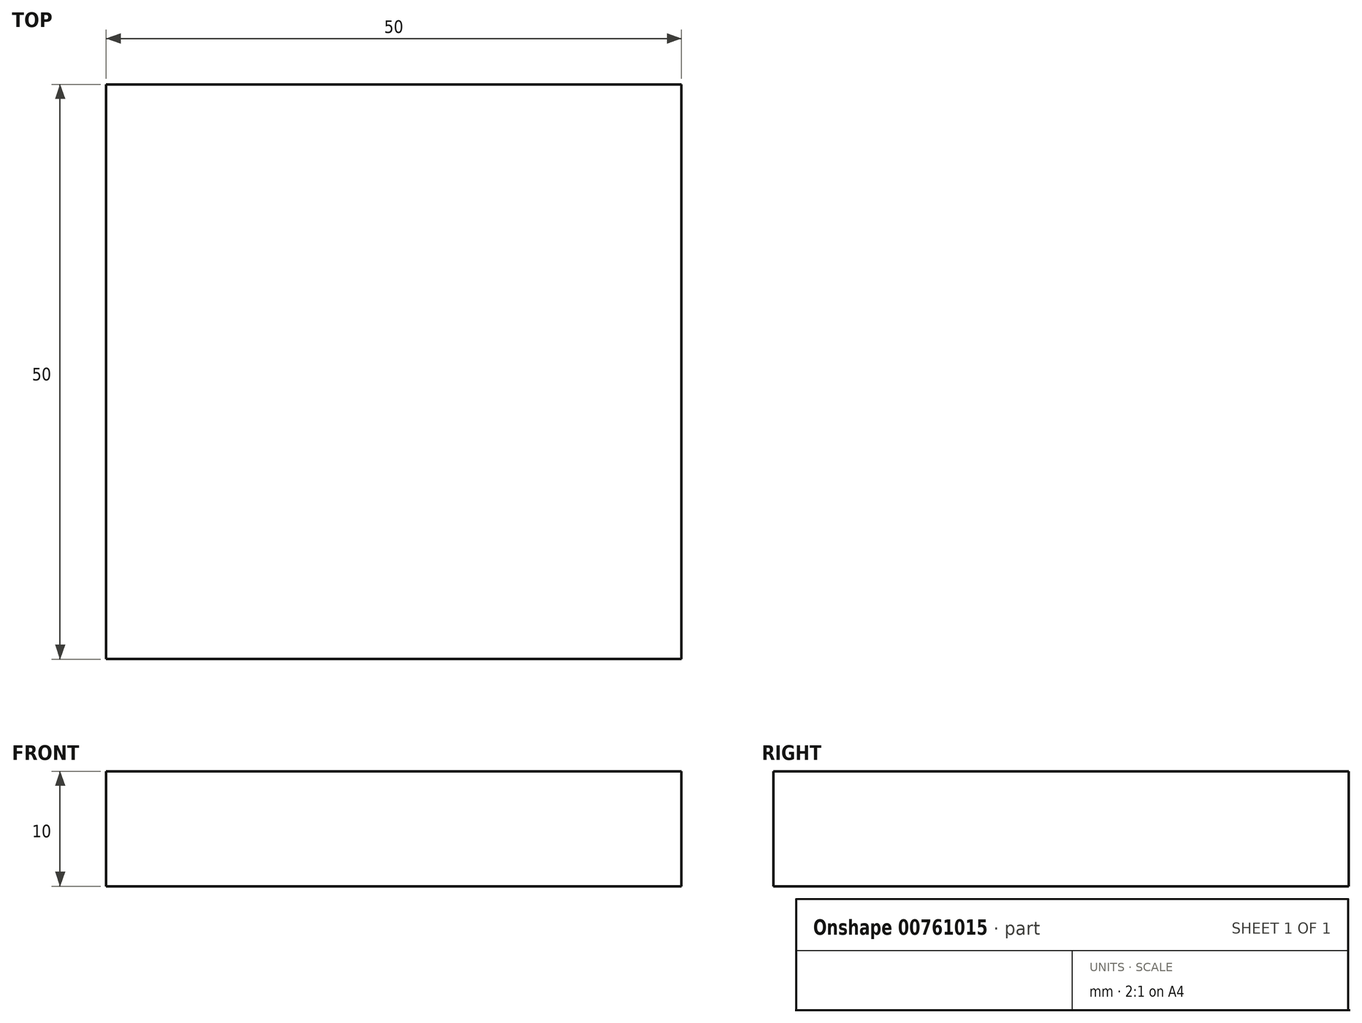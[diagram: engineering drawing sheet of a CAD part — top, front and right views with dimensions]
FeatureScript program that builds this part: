
annotation { "Feature Type Name" : "Feature", "Feature Type Description" : "" }
export const myFeature = defineFeature(function(context is Context, id is Id, definition is map)
    precondition{}
    {
        {
            var Q0;
            Q0=qCreatedBy(makeId("Top.planeOp"),FACE);
            var sketch = newSketch(context, id + "F0", { "sketchPlane" : qUnion([Q0])});
            skLineSegment(sketch, "E0.bottom", {"start": v(-13.93, 17.2) * mm, "end": v(36.07, 17.2) * mm});
            skLineSegment(sketch, "E0.top", {"start": v(-13.93, -32.8) * mm, "end": v(36.07, -32.8) * mm});
            skLineSegment(sketch, "E0.left", {"start": v(-13.93, 17.2) * mm, "end": v(-13.93, -32.8) * mm});
            skLineSegment(sketch, "E0.right", {"start": v(36.07, 17.2) * mm, "end": v(36.07, -32.8) * mm});
            skSolve(sketch);
        }
        {
            var Q0;
            Q0 = qSketchRegion(id + "F0", true);
            extrude(context, id + "F1", {"entities" : qUnion([Q0]), "depth" : 10 * mm, "offsetDistance" : 25 * mm});
        }
    });
